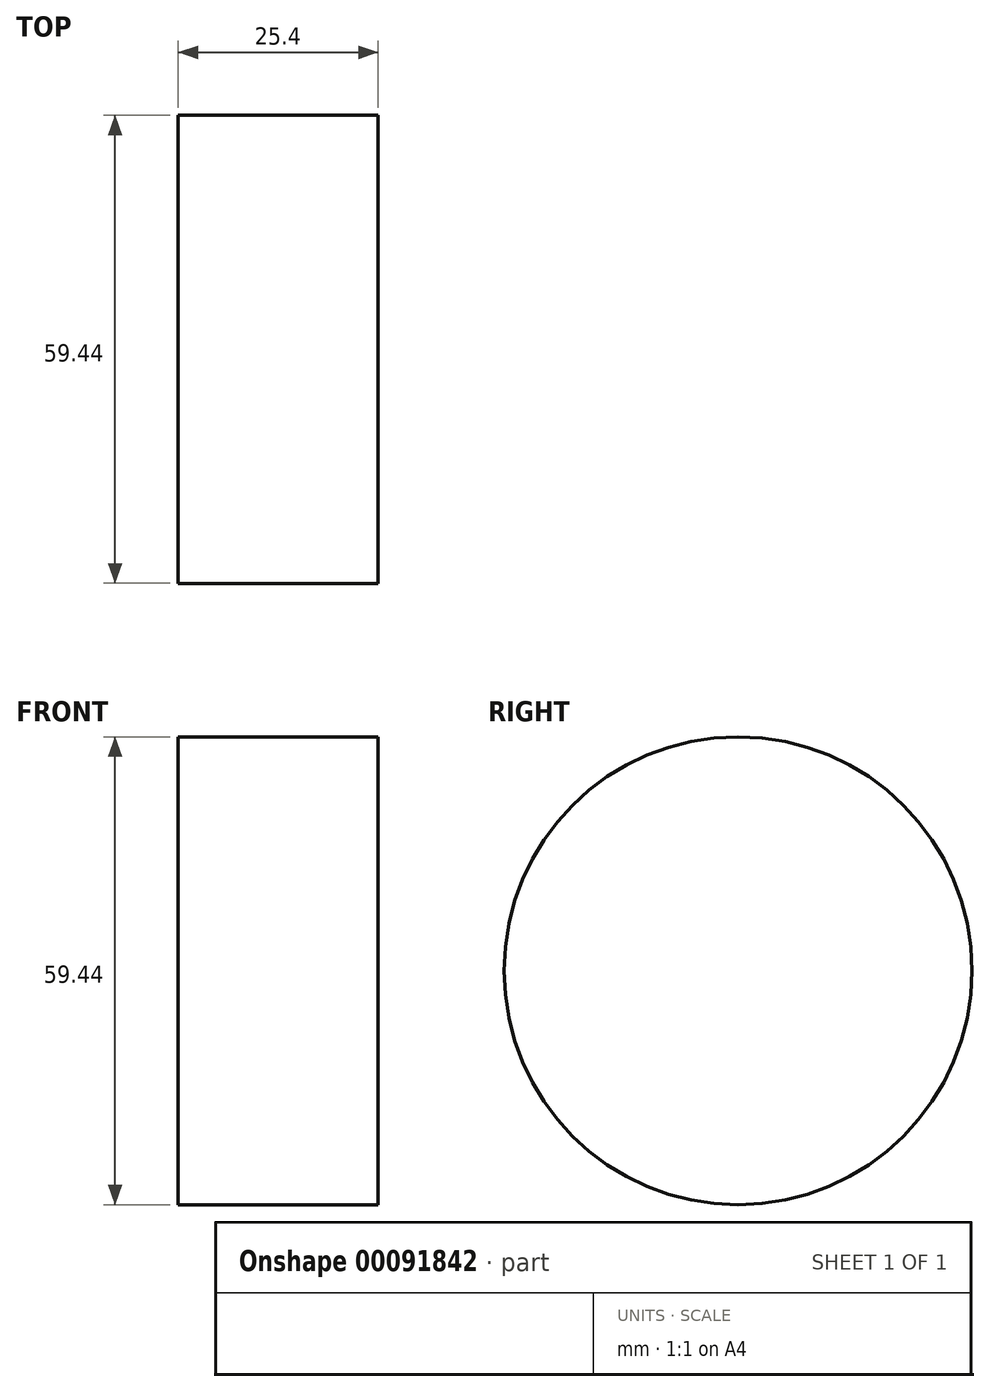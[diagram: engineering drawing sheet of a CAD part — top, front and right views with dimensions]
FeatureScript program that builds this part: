
annotation { "Feature Type Name" : "Feature", "Feature Type Description" : "" }
export const myFeature = defineFeature(function(context is Context, id is Id, definition is map)
    precondition{}
    {
        {
            var Q0;
            Q0=qCreatedBy(makeId("Right.planeOp"),FACE);
            var sketch = newSketch(context, id + "F0", { "sketchPlane" : qUnion([Q0])});
            skCircle(sketch, "E0", {"center": v(0, 0) * mm, "radius": 29.72 * mm});
            skSolve(sketch);
        }
        {
            var Q0;
            Q0=makeQuery(id+"F0.imprint","IMPRINT",FACE,{"disambiguationData":[TD([[makeQuery(id+"F0.imprint","IMPRINT",EDGE,{"derivedFrom":sQuery(id+"F0.wireOp",EDGE,"E0")}),1.0]])]});
            extrude(context, id + "F1", {"entities" : qUnion([Q0]), "depth" : 25.4 * mm});
        }
    });
